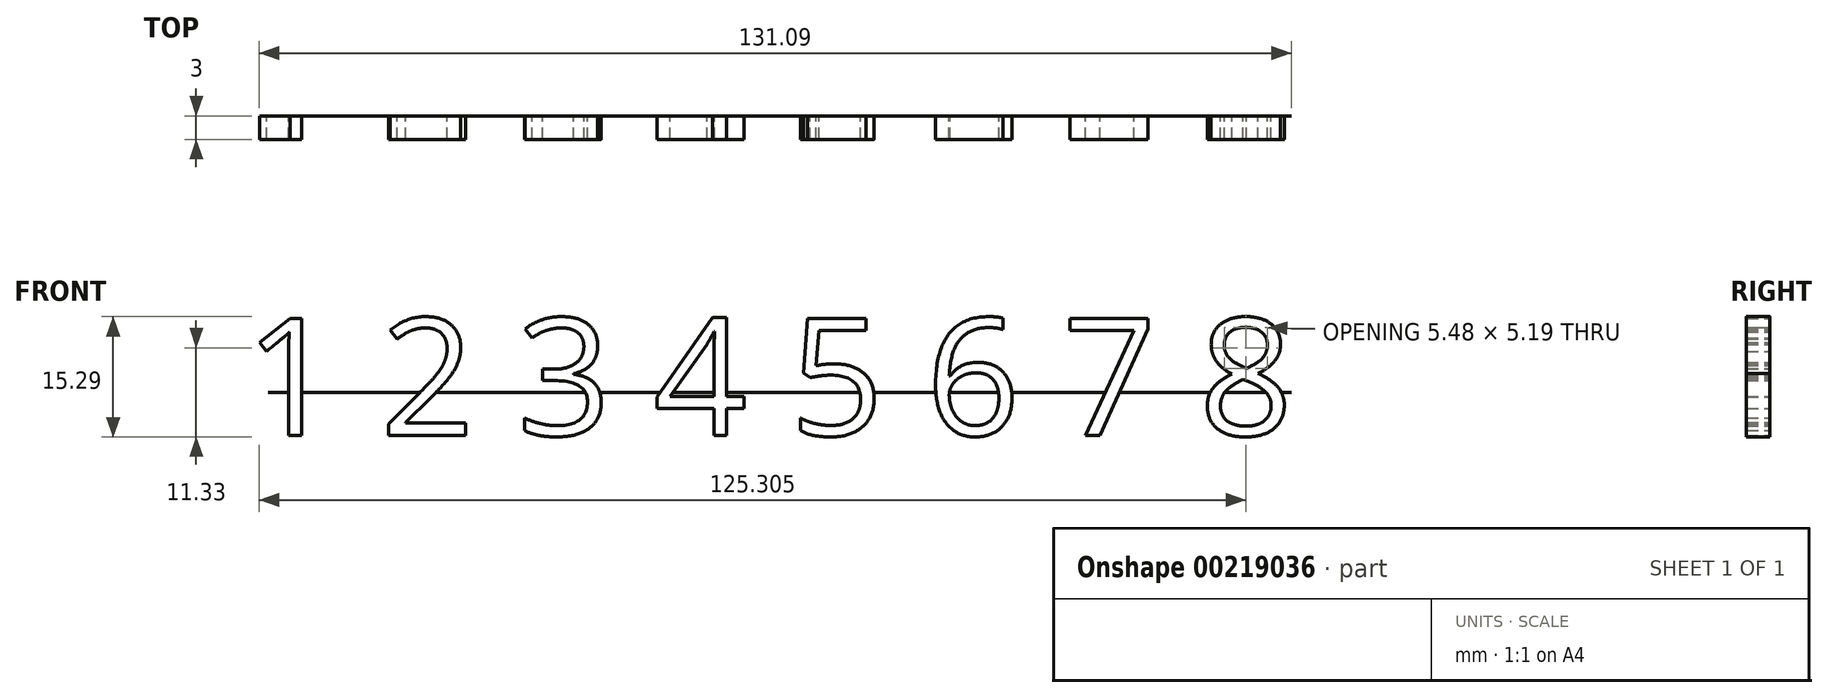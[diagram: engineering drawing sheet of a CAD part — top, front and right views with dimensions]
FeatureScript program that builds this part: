
annotation { "Feature Type Name" : "Feature", "Feature Type Description" : "" }
export const myFeature = defineFeature(function(context is Context, id is Id, definition is map)
    precondition{}
    {
        {
            var Q0;
            Q0=qCreatedBy(makeId("Front.planeOp"),FACE);
            var sketch = newSketch(context, id + "F0", { "sketchPlane" : qUnion([Q0])});
            skText(sketch, "E0", { "text": "1 2 3 4 5 6 7 8", "fontName": "OpenSans-Regular.ttf"});
            const initialGuessF0  = {"E0": [0, 0, 1, 0, 0.015]};
            skSetInitialGuess(sketch, initialGuessF0);
            skSolve(sketch);
        }
        {
            var Q0;
            Q0 = qSketchRegion(id + "F0", true);
            extrude(context, id + "F1", {"entities" : qUnion([Q0]), "depth" : 3 * mm});
        }
        {
            var Q0;
            Q0=qCreatedBy(makeId("Front.planeOp"),FACE);
            var sketch = newSketch(context, id + "F2", { "sketchPlane" : qUnion([Q0])});
            skLineSegment(sketch, "E1.bottom", {"start": v(3, 5.46) * mm, "end": v(133, 5.46) * mm});
            skLineSegment(sketch, "E1.top", {"start": v(3, 5.47) * mm, "end": v(133, 5.47) * mm});
            skLineSegment(sketch, "E1.left", {"start": v(3, 5.46) * mm, "end": v(3, 5.47) * mm});
            skLineSegment(sketch, "E1.right", {"start": v(133, 5.46) * mm, "end": v(133, 5.47) * mm});
            skSolve(sketch);
        }
        {
            var Q0;
            Q0 = qSketchRegion(id + "F2", true);
            extrude(context, id + "F3", {"entities" : qUnion([Q0]), "operationType" : NewBodyOperationType.ADD, "depth" : 0.01 * mm});
        }
    });
